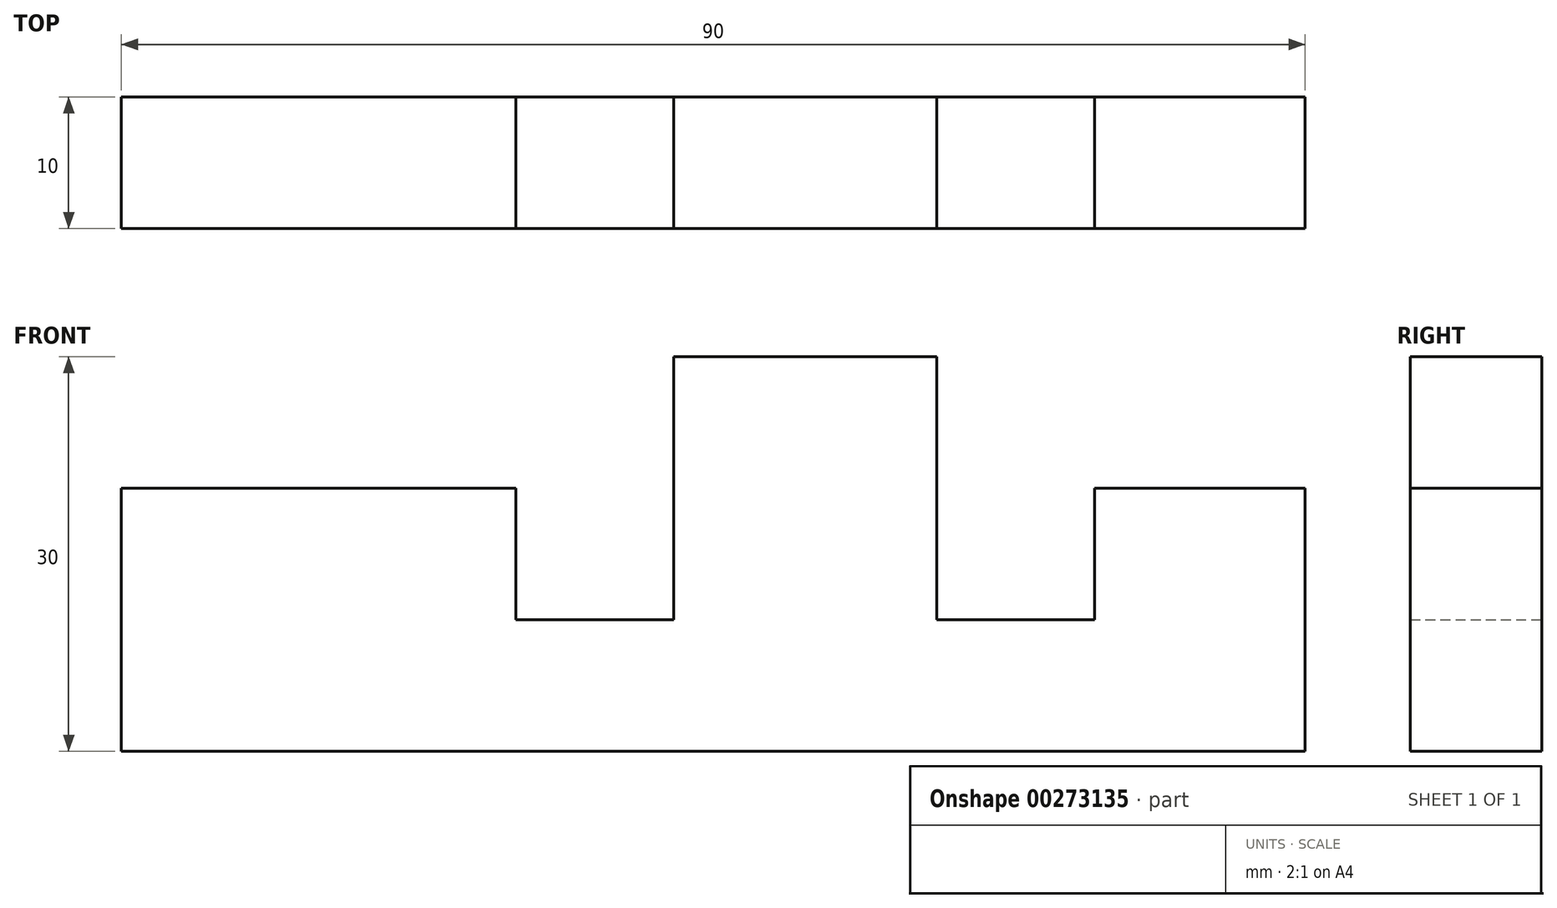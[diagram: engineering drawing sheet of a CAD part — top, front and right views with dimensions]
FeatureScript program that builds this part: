
annotation { "Feature Type Name" : "Feature", "Feature Type Description" : "" }
export const myFeature = defineFeature(function(context is Context, id is Id, definition is map)
    precondition{}
    {
        {
            var Q0;
            Q0=qCreatedBy(makeId("Front.planeOp"),FACE);
            var sketch = newSketch(context, id + "F0", { "sketchPlane" : qUnion([Q0])});
            skLineSegment(sketch, "E0", {"start": v(0, 0) * mm, "end": v(90, 0) * mm});
            skLineSegment(sketch, "E1", {"start": v(0, 0) * mm, "end": v(0, 20) * mm});
            skLineSegment(sketch, "E2", {"start": v(90, 0) * mm, "end": v(90, 20) * mm});
            skLineSegment(sketch, "E3", {"start": v(0, 20) * mm, "end": v(30, 20) * mm});
            skLineSegment(sketch, "E4", {"start": v(30, 20) * mm, "end": v(30, 10) * mm});
            skLineSegment(sketch, "E5", {"start": v(30, 10) * mm, "end": v(42, 10) * mm});
            skLineSegment(sketch, "E6", {"start": v(42, 10) * mm, "end": v(42, 30) * mm});
            skLineSegment(sketch, "E7", {"start": v(42, 30) * mm, "end": v(62, 30) * mm});
            skLineSegment(sketch, "E8", {"start": v(62, 30) * mm, "end": v(62, 10) * mm});
            skLineSegment(sketch, "E9", {"start": v(62, 10) * mm, "end": v(74, 10) * mm});
            skLineSegment(sketch, "E10", {"start": v(74, 10) * mm, "end": v(74, 20) * mm});
            skLineSegment(sketch, "E11", {"start": v(74, 20) * mm, "end": v(90, 20) * mm});
            skSolve(sketch);
        }
        {
            var Q0;
            Q0 = qSketchRegion(id + "F0", true);
            extrude(context, id + "F1", {"entities" : qUnion([Q0]), "depth" : 10 * mm});
        }
    });
